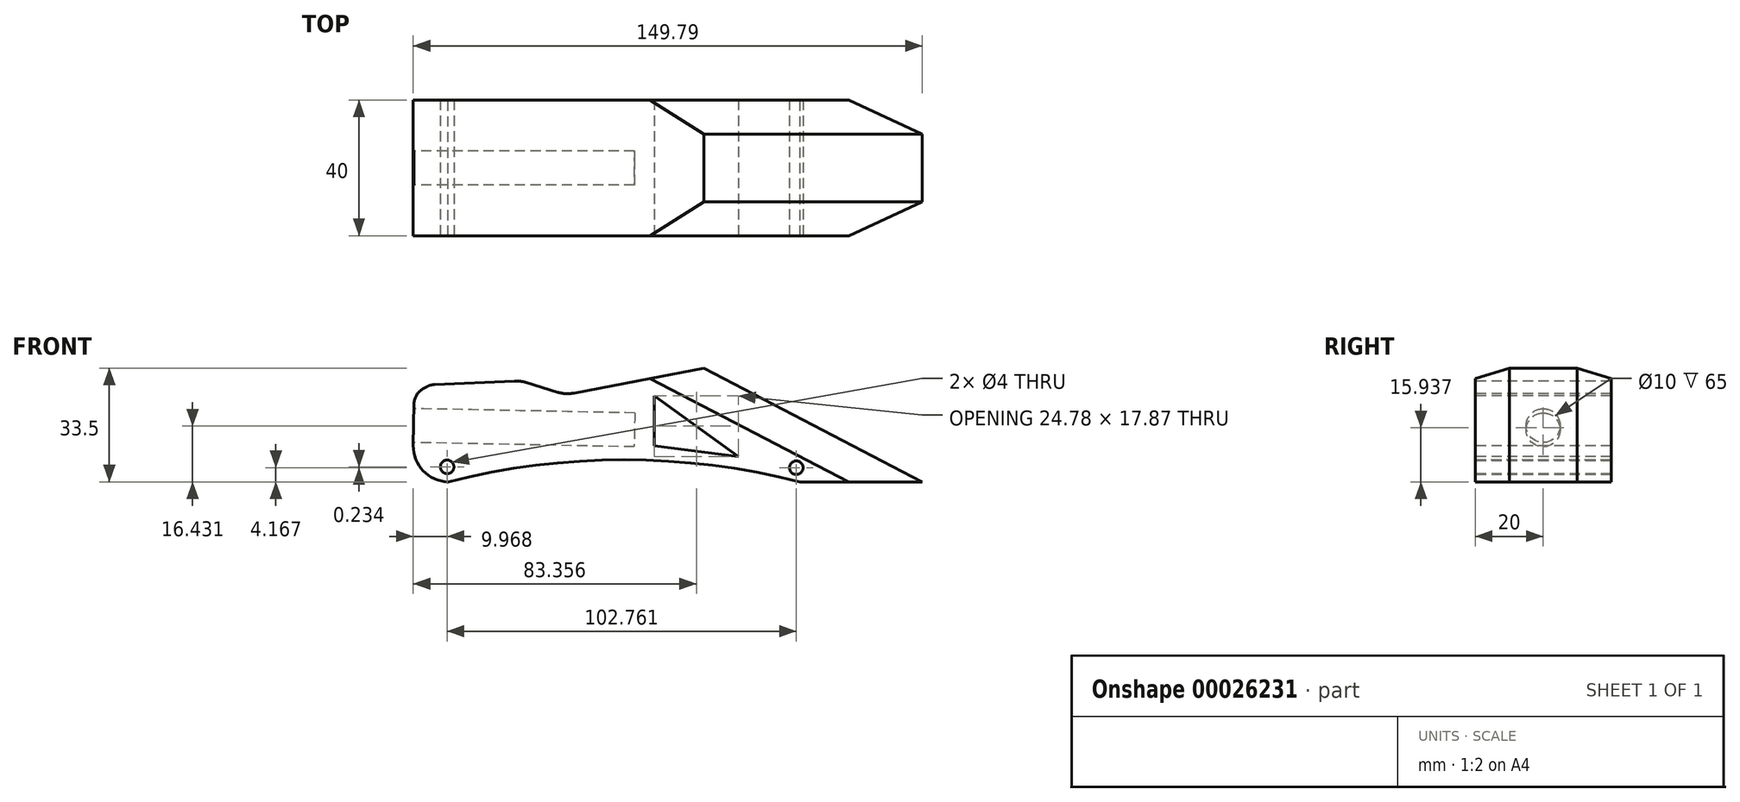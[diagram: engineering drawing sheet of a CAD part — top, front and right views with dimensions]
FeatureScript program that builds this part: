
annotation { "Feature Type Name" : "Feature", "Feature Type Description" : "" }
export const myFeature = defineFeature(function(context is Context, id is Id, definition is map)
    precondition{}
    {
        {
            var Q0;
            Q0=qCreatedBy(makeId("Front.planeOp"),FACE);
            var sketch = newSketch(context, id + "F0", { "sketchPlane" : qUnion([Q0])});
            skLineSegment(sketch, "E0.bottom", {"start": v(8.98, -14.05) * mm, "end": v(146.8, -14.05) * mm});
            skLineSegment(sketch, "E0.left", {"start": v(8.98, -14.05) * mm, "end": v(9.63, 19.32) * mm});
            skLineSegment(sketch, "E1", {"start": v(14.23, 14.57) * mm, "end": v(9.49, 11.86) * mm});
            skLineSegment(sketch, "E2", {"start": v(14.23, 14.57) * mm, "end": v(40.77, 15.72) * mm});
            skLineSegment(sketch, "E3", {"start": v(94.69, 19.45) * mm, "end": v(54.03, 11.62) * mm});
            skLineSegment(sketch, "E4", {"start": v(54.03, 11.62) * mm, "end": v(40.77, 15.72) * mm});
            skArc(sketch, "E5", {"start": v(123.06, -14.05) * mm, "mid": v(71.23, -7.55) * mm, "end": v(19.4, -14.05) * mm});
            skLineSegment(sketch, "E6", {"start": v(94.69, 19.45) * mm, "end": v(158.98, -14.05) * mm});
            skLineSegment(sketch, "E7", {"start": v(158.98, -14.05) * mm, "end": v(146.8, -14.05) * mm});
            skSolve(sketch);
        }
        {
            var Q0;
            Q0=makeQuery(id+"F0.imprint","IMPRINT",FACE,{"disambiguationData":[TD([[makeQuery(id+"F0.imprint","IMPRINT",EDGE,{"derivedFrom":sQuery(id+"F0.wireOp",EDGE,"E0.bottom")}),1.0]])]});
            extrude(context, id + "F1", {"entities" : qUnion([Q0]), "depth" : 40 * mm});
        }
        {
            var Q0;
            Q0=makeQuery(id+"F1.opExtrude","SWEPT_FACE",FACE,{"disambiguationData":[OSD([sQuery(id+"F0.wireOp",EDGE,"E0.left")])]});
            var sketch = newSketch(context, id + "F2", { "sketchPlane" : qUnion([Q0])});
            skCircle(sketch, "E8", {"center": v(20, 2.7) * mm, "radius": 5 * mm});
            skSolve(sketch);
        }
        {
            var Q0;
            Q0=makeQuery(id+"F2.imprint","IMPRINT",FACE,{"disambiguationData":[TD([[makeQuery(id+"F2.imprint","IMPRINT",EDGE,{"derivedFrom":sQuery(id+"F2.wireOp",EDGE,"E8")}),1.0]])]});
            extrude(context, id + "F3", {"entities" : qUnion([Q0]), "operationType" : NewBodyOperationType.REMOVE, "oppositeDirection" : true, "depth" : 65 * mm});
        }
        {
            var Q0;
            Q0=makeQuery(id+"F1.opExtrude","CAP_FACE",FACE,{"disambiguationData":[OSD([sQuery(id+"F0.wireOp",EDGE,"E0.bottom"),sQuery(id+"F0.wireOp",EDGE,"E0.left"),sQuery(id+"F0.wireOp",EDGE,"E1"),sQuery(id+"F0.wireOp",EDGE,"E2"),sQuery(id+"F0.wireOp",EDGE,"E3"),sQuery(id+"F0.wireOp",EDGE,"E4"),sQuery(id+"F0.wireOp",EDGE,"E5"),sQuery(id+"F0.wireOp",EDGE,"E6"),sQuery(id+"F0.wireOp",EDGE,"E7")])],"isStart":false});
            var sketch = newSketch(context, id + "F4", { "sketchPlane" : qUnion([Q0])});
            skCircle(sketch, "E9", {"center": v(19.16, -9.65) * mm, "radius": 2 * mm});
            skCircle(sketch, "E10", {"center": v(121.92, -9.88) * mm, "radius": 2 * mm});
            skSolve(sketch);
        }
        {
            var Q0;
            Q0 = qSketchRegion(id + "F4", true);
            extrude(context, id + "F5", {"entities" : qUnion([Q0]), "operationType" : NewBodyOperationType.REMOVE, "endBound" : BoundingType.THROUGH_ALL, "oppositeDirection" : true, "depth" : 25 * mm});
        }
        {
            var Q0;
            Q0=makeQuery(id+"F1.opExtrude","CAP_EDGE",EDGE,{"disambiguationData":[OSD([sQuery(id+"F0.wireOp",EDGE,"E6")])],"isStart":false});
            var Q1;
            Q1=makeQuery(id+"F1.opExtrude","CAP_EDGE",EDGE,{"disambiguationData":[OSD([sQuery(id+"F0.wireOp",EDGE,"E6")])],"isStart":true});
            chamfer(context, id + "F6", {"entities" : qUnion([Q0, Q1]), "width" : 10 * mm, "tangentPropagation" : true});
        }
        {
            var Q0;
            Q0=makeQuery(id+"F1.opExtrude","SWEPT_EDGE",EDGE,{"disambiguationData":[OSD([sQuery(id+"F0.wireOp",EDGE,"E0.bottom"),sQuery(id+"F0.wireOp",EDGE,"E0.left")])]});
            fillet(context, id + "F7", {"entities" : qUnion([Q0]), "radius" : 10.5 * mm, "tangentPropagation" : true, "allowEdgeOverflow" : false});
        }
        {
            var Q0;
            Q0=makeQuery(id+"F1.opExtrude","SWEPT_EDGE",EDGE,{"disambiguationData":[OSD([sQuery(id+"F0.wireOp",EDGE,"E2"),sQuery(id+"F0.wireOp",EDGE,"E4")])]});
            var Q1;
            Q1=makeQuery(id+"F1.opExtrude","SWEPT_EDGE",EDGE,{"disambiguationData":[OSD([sQuery(id+"F0.wireOp",EDGE,"E3"),sQuery(id+"F0.wireOp",EDGE,"E4")])]});
            fillet(context, id + "F8", {"entities" : qUnion([Q0, Q1]), "radius" : 10 * mm, "tangentPropagation" : true, "allowEdgeOverflow" : false});
        }
        {
            var Q0;
            Q0=makeQuery(id+"F1.opExtrude","SWEPT_EDGE",EDGE,{"disambiguationData":[OSD([sQuery(id+"F0.wireOp",EDGE,"E0.left"),sQuery(id+"F0.wireOp",EDGE,"E1")])]});
            var Q1;
            Q1=makeQuery(id+"F1.opExtrude","SWEPT_EDGE",EDGE,{"disambiguationData":[OSD([sQuery(id+"F0.wireOp",EDGE,"E1"),sQuery(id+"F0.wireOp",EDGE,"E2")])]});
            fillet(context, id + "F9", {"entities" : qUnion([Q0, Q1]), "radius" : 5 * mm, "tangentPropagation" : true, "allowEdgeOverflow" : false});
        }
        {
            var Q0;
            Q0=makeQuery(id+"F1.opExtrude","CAP_FACE",FACE,{"disambiguationData":[OSD([sQuery(id+"F0.wireOp",EDGE,"E0.bottom"),sQuery(id+"F0.wireOp",EDGE,"E0.left"),sQuery(id+"F0.wireOp",EDGE,"E1"),sQuery(id+"F0.wireOp",EDGE,"E2"),sQuery(id+"F0.wireOp",EDGE,"E3"),sQuery(id+"F0.wireOp",EDGE,"E4"),sQuery(id+"F0.wireOp",EDGE,"E5"),sQuery(id+"F0.wireOp",EDGE,"E6"),sQuery(id+"F0.wireOp",EDGE,"E7")])],"isStart":false});
            var sketch = newSketch(context, id + "F10", { "sketchPlane" : qUnion([Q0])});
            skSolve(sketch);
        }
        {
            var Q0;
            {var subQ6=sQuery(id+"F0.wireOp",EDGE,"E5");Q0=makeQuery(id+"F10.imprint","IMPRINT",FACE,{"disambiguationData":[TD([[makeQuery(id+"F10.imprint","IMPRINT",EDGE,{"derivedFrom":makeQuery(id+"F1.opExtrude","CAP_EDGE",EDGE,{"disambiguationData":[OSD([subQ6])],"isStart":false})}),-1.0]])]});}
            var sketch = newSketch(context, id + "F11", { "sketchPlane" : qUnion([Q0])});
            skLineSegment(sketch, "E11", {"start": v(80.15, 11.31) * mm, "end": v(80.15, -3.48) * mm});
            skLineSegment(sketch, "E12", {"start": v(80.15, -3.48) * mm, "end": v(104.94, -6.55) * mm});
            skLineSegment(sketch, "E13", {"start": v(104.94, -6.55) * mm, "end": v(80.15, 11.31) * mm});
            skSolve(sketch);
        }
        {
            var Q0;
            Q0 = qSketchRegion(id + "F11", true);
            extrude(context, id + "F12", {"entities" : qUnion([Q0]), "operationType" : NewBodyOperationType.REMOVE, "endBound" : BoundingType.THROUGH_ALL, "oppositeDirection" : true, "depth" : 25 * mm});
        }
    });
